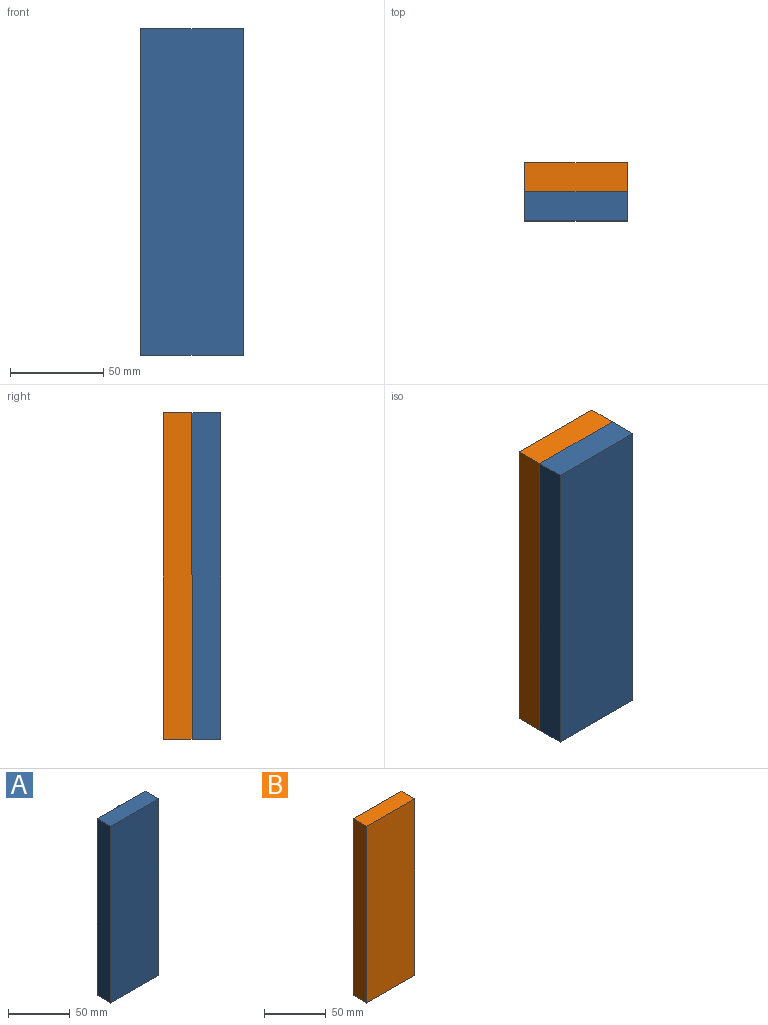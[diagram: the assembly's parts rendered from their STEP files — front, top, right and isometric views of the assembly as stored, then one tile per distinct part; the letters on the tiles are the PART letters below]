
ASSEMBLY  parts=2 mates=1
PART A: 23 faces, bbox 55x18.5x175 mm
  f0: plane 35x8mm, normal (0,0,-1), area 277.2mm2, adj f1,f2,f3,f4,f5,f13
  f1: plane 45x6.04mm, normal (-1,0.02,0), area 271.6mm2, adj f0,f2,f6,f13
  f2: cylinder r=2mm len=45mm, axis (0,0,1), area 139.8mm2, adj f0,f1,f3,f6
  f3: plane 45x30.79mm, normal (0,1,0), area 1385.5mm2, adj f0,f2,f4,f6
  f4: cylinder r=2mm len=45mm, axis (0,0,-1), area 139.8mm2, adj f0,f3,f5,f6
  f5: plane 45x6.04mm, normal (1,0.02,0), area 271.6mm2, adj f0,f4,f6,f13
  f6: plane 40x10.5mm, normal (0,0,-1), area 139.2mm2, adj f1,f2,f3,f4,f5,f7,f8,f9
  f7: plane 110x8.54mm, normal (1,0.02,0), area 939mm2, adj f6,f10,f11,f13
  f8: plane 110x35.7mm, normal (0,1,0), area 3927.3mm2, adj f6,f10,f11,f12
  f9: plane 110x8.54mm, normal (-1,0.02,0), area 939mm2, adj f6,f10,f12,f13
  f10: plane 40x10.5mm, normal (0,0,1), area 416.4mm2, adj f7,f8,f9,f11,f12,f13
  f11: cylinder r=2mm len=110mm, axis (0,0,-1), area 341.7mm2, adj f6,f7,f8,f10
  f12: cylinder r=2mm len=110mm, axis (0,0,1), area 341.7mm2, adj f6,f8,f9,f10
  f13: plane 175x55mm, normal (0,1,0), area 3573mm2, adj f0,f1,f5,f6,f7,f9,f10,f14
  f14: plane 55x15.5mm, normal (0,0,1), area 852.5mm2, adj f13,f15,f16,f17
  f15: plane 175x15.5mm, normal (1,0,0), area 2712.5mm2, adj f13,f14,f16,f18
  f16: plane 175x55mm, normal (0,-1,0), area 9625mm2, adj f14,f15,f17,f18
  f17: plane 175x15.5mm, normal (-1,0,0), area 2712.5mm2, adj f13,f14,f16,f18
  f18: plane 55x15.5mm, normal (0,0,-1), area 852.5mm2, adj f13,f15,f16,f17
  f19: cone r=3.5mm half-angle=3deg, axis (0,-1,0), area 64.6mm2, adj f13,f20
  f20: plane 6.69x6.69mm, normal (0,1,0), area 35.1mm2, adj f19
  f21: cone r=3.5mm half-angle=3deg, axis (0,-1,0), area 64.6mm2, adj f13,f22
  f22: plane 6.69x6.69mm, normal (0,1,0), area 35.1mm2, adj f21
PART B: 23 faces, bbox 55x15.5x175 mm
  f0: plane 35x8mm, normal (0,0,-1), area 277.2mm2, adj f1,f2,f3,f4,f5,f13
  f1: plane 45x6.04mm, normal (-1,0.02,0), area 271.6mm2, adj f0,f2,f6,f13
  f2: cylinder r=2mm len=45mm, axis (0,0,1), area 139.8mm2, adj f0,f1,f3,f6
  f3: plane 45x30.79mm, normal (0,1,0), area 1385.5mm2, adj f0,f2,f4,f6
  f4: cylinder r=2mm len=45mm, axis (0,0,-1), area 139.8mm2, adj f0,f3,f5,f6
  f5: plane 45x6.04mm, normal (1,0.02,0), area 271.6mm2, adj f0,f4,f6,f13
  f6: plane 40x10.5mm, normal (0,0,-1), area 139.2mm2, adj f1,f2,f3,f4,f5,f7,f8,f9
  f7: plane 110x8.54mm, normal (1,0.02,0), area 939mm2, adj f6,f10,f11,f13
  f8: plane 110x35.7mm, normal (0,1,0), area 3927.3mm2, adj f6,f10,f11,f12
  f9: plane 110x8.54mm, normal (-1,0.02,0), area 939mm2, adj f6,f10,f12,f13
  f10: plane 40x10.5mm, normal (0,0,1), area 416.4mm2, adj f7,f8,f9,f11,f12,f13
  f11: cylinder r=2mm len=110mm, axis (0,0,-1), area 341.7mm2, adj f6,f7,f8,f10
  f12: cylinder r=2mm len=110mm, axis (0,0,1), area 341.7mm2, adj f6,f8,f9,f10
  f13: plane 175x55mm, normal (0,1,0), area 3561.6mm2, adj f0,f1,f5,f6,f7,f9,f10,f14
  f14: plane 55x15.5mm, normal (0,0,1), area 852.5mm2, adj f13,f15,f16,f17
  f15: plane 175x15.5mm, normal (1,0,0), area 2712.5mm2, adj f13,f14,f16,f18
  f16: plane 175x55mm, normal (0,-1,0), area 9625mm2, adj f14,f15,f17,f18
  f17: plane 175x15.5mm, normal (-1,0,0), area 2712.5mm2, adj f13,f14,f16,f18
  f18: plane 55x15.5mm, normal (0,0,-1), area 852.5mm2, adj f13,f15,f16,f17
  f19: cone r=3.75mm half-angle=3deg, axis (0,1,0), area 80.6mm2, adj f13,f20
  f20: plane 7.13x7.13mm, normal (0,1,0), area 40mm2, adj f19
  f21: cone r=3.75mm half-angle=3deg, axis (0,1,0), area 80.6mm2, adj f13,f22
  f22: plane 7.13x7.13mm, normal (0,1,0), area 40mm2, adj f21
PLACE A t=(-32.06,17.66,-12.99)mm
PLACE B rot(axis=(0,0,-1),180deg) t=(-32.06,17.66,-12.99)mm
MATE planar B.f14 <-> A.f14  axis (0,0,1) through (-32.06,25.41,42.01)mm
